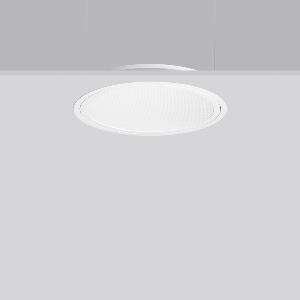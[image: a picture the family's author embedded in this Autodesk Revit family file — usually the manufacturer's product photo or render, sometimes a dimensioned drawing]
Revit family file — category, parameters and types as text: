
# Revit family: triona_round_e_312423_002_12_6f03
name_source: partatom
category: Lighting Fixtures
units: mm (PartAtom-declared; Revit-internal decimal feet)

## family parameters
Cut with Voids When Loaded = No
Host = Face
Light Source = No
Part Type = Normal
Room Calculation Point = No
Round Connector Dimension = Use Diameter
Shared = No

## types (1)
- TRIONA round E (1 x LED Modul 830, 3150 lm, 3000)
    Apparent Load = 28 VA
    CIE Flux Codes = 58 87 97 100 100
    Color Rendering = 80
    Color Temperature = 3000
    Default Elevation = 1800 mm
    Description = Series: TRIONA round
Decorative round LED recessed surface luminaire. Cover made of sheet steel, powder-coated. Frame made of aluminium, powder-coated. Recessed ring: aluminium extrusion profile, powder coated. Light emission through a diffuser in plastic, opal/prismatic. Lightguide and diffuser made of non-yellowing plastic (PMMA). Lateral light emission (RZB SIDELITE technology) for above-average homogeneous light distribution. Suitable for installation in cavity ceilings. Tool-free mounting system thanks to the rocker arm mechanism (patent pending). Electronic ballast included. Very easy installation thanks to Plug+Play connection. 
Colour: traffic white, matt (RAL 9016)
Diameter: 505 mm
Height: 2 mm
Cut-out diameter: 482 mm
Recess height: 100 mm
Luminaire: recess height: 89 mm
Lamp: LED
Socket: without socket
Colour temperature: 3000K
Colour rendering index (CRI): 80
System power: 28 W
Rated luminous flux: 3150 lm
Luminous efficiency: 113 lm/W
Control gear: Converter, dimmable, DALI
Protection class: I
Type of protection: IP 40
    Height = 0 mm  [stored 0 ft]
    Lamp = 1 x LED Modul 830
    Lamp Light Flux = 3150 lm
    Lamp count = 1
    Length = 505 mm
    Lifetime = 50000 h
    Luminous efficacy = 113 lm/W
    Manufacturer = RZB
    ModVariant = No
    Model = 312423.002.12
    Mounting Place = Ceiling
    Mounting Type = Recessed
    Number of Poles = 1
    OnlyDefault = Yes
    Power Factor = 1
    Product Name = TRIONA round E
    Product group = Recessed modular luminaires
    ProductGroupID = 406
    Protection Class = Protection class I
    Protection Degree = IP 20
    RLX_Detail_Level = 1
    RLX_Emergency_Light_Flux = 0 lm
    RLX_Emergency_Type = 0
    RLX_Emergency_Type_DB = No
    RlxData = <blob elided: 31193 chars, md5=54587b7a>
    Socket = socket
    Standby Power = 0 W
    System Light Flux = 3150 lm
    System Power = 28 W
    Type Comments = Product without accessories
    Type Image = 312423.002.12.jpg
    URL = http://relux.com
    VarID = ---
    Voltage = 230 V
    Voltage Range = 220-240 V
    Weight = 0.00 kg
    Width = 0 mm  [stored 0 ft]

note: [stored X ft] marks values corroborated as IEEE doubles in the binary element streams (Revit-internal decimal feet)

## geometry (parser evidence)
native form markers: Blend x4, Sweep x9
no freeform markers — native parametric forms only
